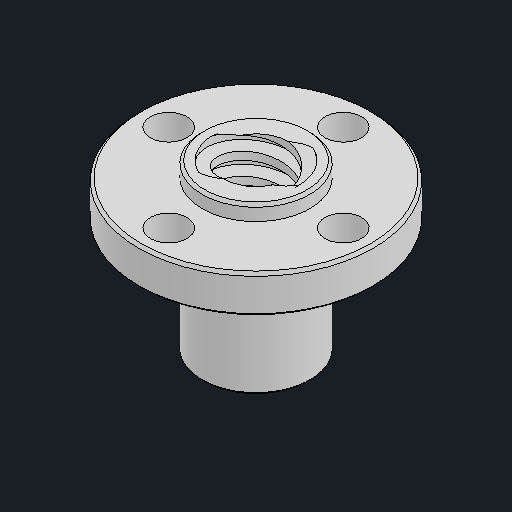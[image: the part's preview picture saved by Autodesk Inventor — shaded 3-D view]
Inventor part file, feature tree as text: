
AUTODESK INVENTOR PART (.ipt)
format: ipt  version: 2024.2 (Build 282272000, 272)  size: 301,056 bytes
history: native  units: mm
features: other x1, chamfer x1
ambient origin geometry x8: Origin, YZ Plane, XZ Plane, XY Plane, X Axis, Y Axis, Z Axis, Center Point
bodies: Body1 (feature_tree)
feature tree (2):
  other  "솔리드1"
  chamfer  "Chamfer1"  [1 undecoded]
note: 1 required parameter value undecoded (feature->parameter linkage not recoverable at this tier; creation-order binding heuristic only, values carry confidence <= 0.55)
